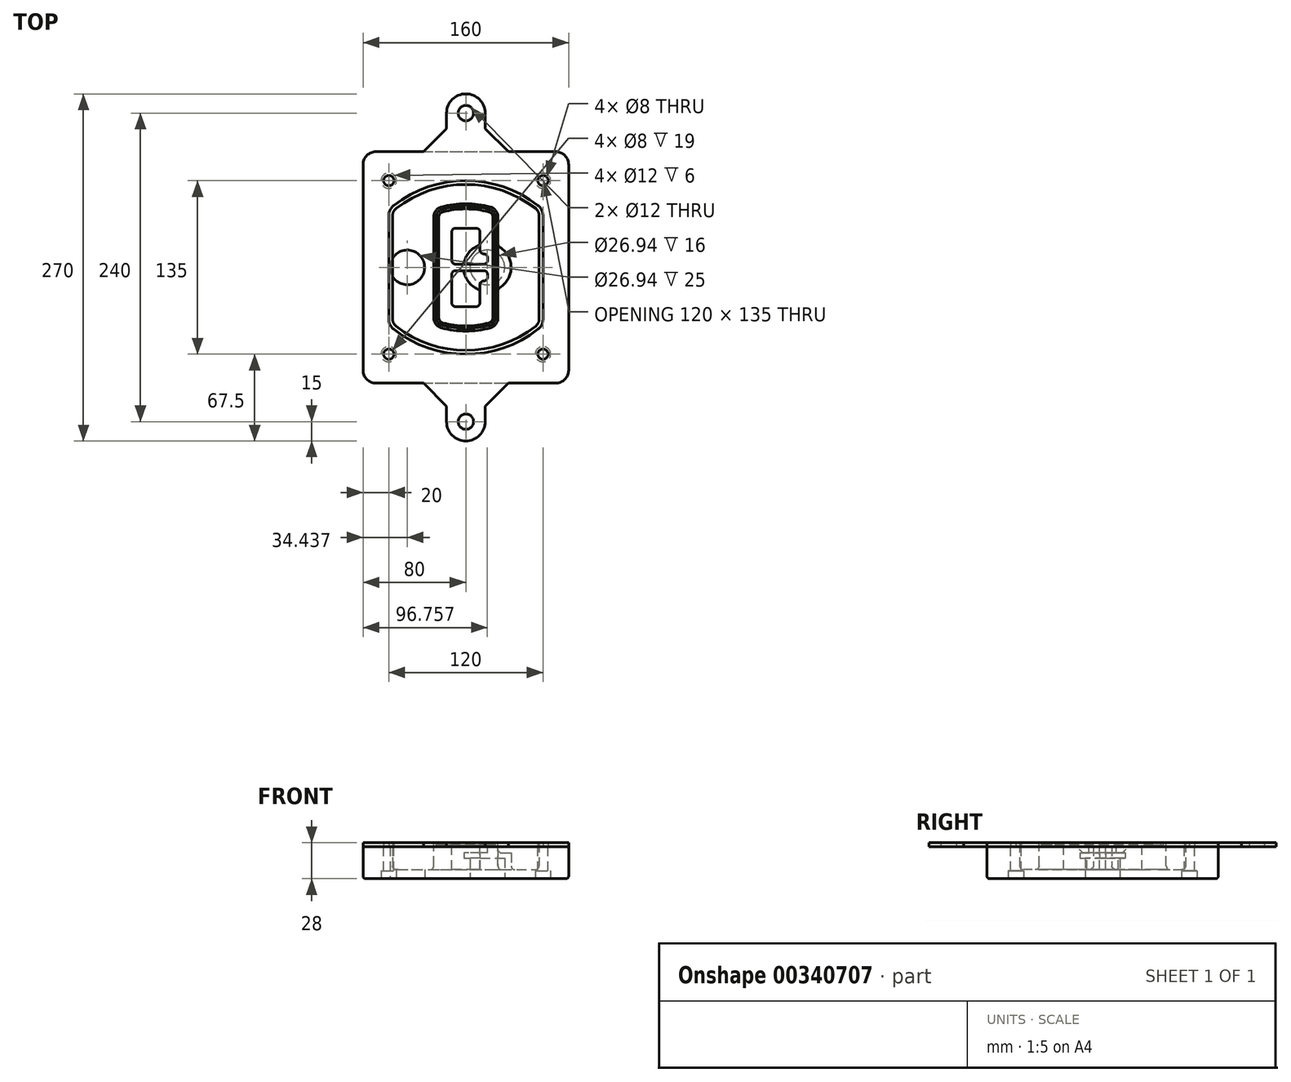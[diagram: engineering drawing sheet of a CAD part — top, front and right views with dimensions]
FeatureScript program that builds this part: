
annotation { "Feature Type Name" : "Feature", "Feature Type Description" : "" }
export const myFeature = defineFeature(function(context is Context, id is Id, definition is map)
    precondition{}
    {
        {
            var Q0;
            Q0=qCreatedBy(makeId("Top.planeOp"),FACE);
            var sketch = newSketch(context, id + "F0", { "sketchPlane" : qUnion([Q0])});
            skPoint(sketch, "E0.rect.middle", {"position": v(0, 0) * mm});
            skLineSegment(sketch, "E1.bottom", {"start": v(-70, -90) * mm, "end": v(70, -90) * mm});
            skLineSegment(sketch, "E1.top", {"start": v(-70, 90) * mm, "end": v(70, 90) * mm});
            skLineSegment(sketch, "E1.left", {"start": v(-80, -80) * mm, "end": v(-80, 80) * mm});
            skLineSegment(sketch, "E1.right", {"start": v(80, -80) * mm, "end": v(80, 80) * mm});
            skLineSegment(sketch, "E2", {"start": v(-80, 90) * mm, "end": v(80, -90) * mm, "construction": true});
            skLineSegment(sketch, "E3", {"start": v(80, 90) * mm, "end": v(-80, -90) * mm, "construction": true});
            skCircle(sketch, "E4", {"center": v(-60, 67.5) * mm, "radius": 4 * mm});
            skCircle(sketch, "E5", {"center": v(60, 67.5) * mm, "radius": 4 * mm});
            skCircle(sketch, "E6", {"center": v(60, -67.5) * mm, "radius": 4 * mm});
            skCircle(sketch, "E7", {"center": v(-60, -67.5) * mm, "radius": 4 * mm});
            skLineSegment(sketch, "E8", {"start": v(-60, 67.5) * mm, "end": v(60, 67.5) * mm, "construction": true});
            skLineSegment(sketch, "E9", {"start": v(60, 67.5) * mm, "end": v(60, -67.5) * mm, "construction": true});
            skLineSegment(sketch, "E10", {"start": v(60, -67.5) * mm, "end": v(-60, -67.5) * mm, "construction": true});
            skLineSegment(sketch, "E11", {"start": v(-60, -67.5) * mm, "end": v(-60, 67.5) * mm, "construction": true});
            skLineSegment(sketch, "E12", {"start": v(-60, 40.3) * mm, "end": v(-60, -40.3) * mm});
            skLineSegment(sketch, "E13", {"start": v(60, 40.3) * mm, "end": v(60, -40.3) * mm});
            skArc(sketch, "E14", {"start": v(56.15, 48.18) * mm, "mid": v(0, 67.5) * mm, "end": v(-56.15, 48.18) * mm});
            skArc(sketch, "E15", {"start": v(-56.15, -48.18) * mm, "mid": v(0, -67.5) * mm, "end": v(56.15, -48.18) * mm});
            skLineSegment(sketch, "E16", {"start": v(-60, 0) * mm, "end": v(60, 0) * mm, "construction": true});
            skPoint(sketch, "E17.visualSharp", {"position": v(-60, -45) * mm});
            skArc(sketch, "E17.filletArc", {"start": v(-60, -40.3) * mm, "mid": v(-58.99, -44.68) * mm, "end": v(-56.15, -48.18) * mm});
            skPoint(sketch, "E18.visualSharp", {"position": v(-60, 45) * mm});
            skArc(sketch, "E18.filletArc", {"start": v(-56.15, 48.18) * mm, "mid": v(-58.99, 44.68) * mm, "end": v(-60, 40.3) * mm});
            skPoint(sketch, "E19.visualSharp", {"position": v(60, 45) * mm});
            skArc(sketch, "E19.filletArc", {"start": v(60, 40.3) * mm, "mid": v(58.99, 44.68) * mm, "end": v(56.15, 48.18) * mm});
            skPoint(sketch, "E20.visualSharp", {"position": v(60, -45) * mm});
            skArc(sketch, "E20.filletArc", {"start": v(56.15, -48.18) * mm, "mid": v(58.99, -44.68) * mm, "end": v(60, -40.3) * mm});
            skPoint(sketch, "E21.visualSharp", {"position": v(-80, 90) * mm});
            skArc(sketch, "E21.filletArc", {"start": v(-70, 90) * mm, "mid": v(-77.07, 87.07) * mm, "end": v(-80, 80) * mm});
            skPoint(sketch, "E22.visualSharp", {"position": v(80, 90) * mm});
            skArc(sketch, "E22.filletArc", {"start": v(80, 80) * mm, "mid": v(77.07, 87.07) * mm, "end": v(70, 90) * mm});
            skPoint(sketch, "E23.visualSharp", {"position": v(80, -90) * mm});
            skArc(sketch, "E23.filletArc", {"start": v(70, -90) * mm, "mid": v(77.07, -87.07) * mm, "end": v(80, -80) * mm});
            skPoint(sketch, "E24.visualSharp", {"position": v(-80, -90) * mm});
            skArc(sketch, "E24.filletArc", {"start": v(-80, -80) * mm, "mid": v(-77.07, -87.07) * mm, "end": v(-70, -90) * mm});
            skArc(sketch, "E25.0", {"start": v(57, 40.3) * mm, "mid": v(56.3, 43.36) * mm, "end": v(54.3, 45.81) * mm});
            skLineSegment(sketch, "E25.1", {"start": v(57, 40.3) * mm, "end": v(57, -40.3) * mm});
            skArc(sketch, "E25.2", {"start": v(54.3, -45.81) * mm, "mid": v(56.3, -43.36) * mm, "end": v(57, -40.3) * mm});
            skArc(sketch, "E25.3", {"start": v(-54.3, -45.81) * mm, "mid": v(0, -64.5) * mm, "end": v(54.3, -45.81) * mm});
            skArc(sketch, "E25.4", {"start": v(-57, -40.3) * mm, "mid": v(-56.3, -43.36) * mm, "end": v(-54.3, -45.81) * mm});
            skArc(sketch, "E25.5", {"start": v(54.3, 45.81) * mm, "mid": v(0, 64.5) * mm, "end": v(-54.3, 45.81) * mm});
            skLineSegment(sketch, "E25.6", {"start": v(-57, 40.3) * mm, "end": v(-57, -40.3) * mm});
            skArc(sketch, "E25.7", {"start": v(-54.3, 45.81) * mm, "mid": v(-56.3, 43.36) * mm, "end": v(-57, 40.3) * mm});
            skArc(sketch, "E26.0", {"start": v(-58.62, 51.33) * mm, "mid": v(-62.58, 46.43) * mm, "end": v(-64, 40.3) * mm});
            skArc(sketch, "E26.1", {"start": v(58.62, 51.33) * mm, "mid": v(0, 71.5) * mm, "end": v(-58.62, 51.33) * mm});
            skArc(sketch, "E26.2", {"start": v(64, 40.3) * mm, "mid": v(62.58, 46.43) * mm, "end": v(58.62, 51.33) * mm});
            skLineSegment(sketch, "E26.3", {"start": v(64, 40.3) * mm, "end": v(64, -40.3) * mm});
            skArc(sketch, "E26.4", {"start": v(58.62, -51.33) * mm, "mid": v(62.58, -46.43) * mm, "end": v(64, -40.3) * mm});
            skLineSegment(sketch, "E26.5", {"start": v(-64, 40.3) * mm, "end": v(-64, -40.3) * mm});
            skArc(sketch, "E26.6", {"start": v(-58.62, -51.33) * mm, "mid": v(0, -71.5) * mm, "end": v(58.62, -51.33) * mm});
            skArc(sketch, "E26.7", {"start": v(-64, -40.3) * mm, "mid": v(-62.58, -46.43) * mm, "end": v(-58.62, -51.33) * mm});
            skSolve(sketch);
        }
        {
            var Q0;
            Q0=makeQuery(id+"F0.imprint","IMPRINT",FACE,{"disambiguationData":[TD([[makeQuery(id+"F0.imprint","IMPRINT",EDGE,{"derivedFrom":sQuery(id+"F0.wireOp",EDGE,"E1.bottom")}),1.0]])]});
            var Q1;
            Q1=makeQuery(id+"F0.imprint","IMPRINT",FACE,{"disambiguationData":[TD([[makeQuery(id+"F0.imprint","IMPRINT",EDGE,{"derivedFrom":sQuery(id+"F0.wireOp",EDGE,"E12")}),1.0]])]});
            var Q2;
            Q2=makeQuery(id+"F0.imprint","IMPRINT",FACE,{"disambiguationData":[TD([[makeQuery(id+"F0.imprint","IMPRINT",EDGE,{"derivedFrom":sQuery(id+"F0.wireOp",EDGE,"E25.0")}),1.0]])]});
            var Q3;
            Q3=makeQuery(id+"F0.imprint","IMPRINT",FACE,{"disambiguationData":[TD([[makeQuery(id+"F0.imprint","IMPRINT",EDGE,{"derivedFrom":sQuery(id+"F0.wireOp",EDGE,"E12")}),-1.0]])]});
            extrude(context, id + "F1", {"entities" : qUnion([Q0, Q1, Q2, Q3]), "oppositeDirection" : true, "depth" : 25 * mm});
        }
        {
            var Q0;
            Q0=makeQuery(id+"F0.imprint","IMPRINT",FACE,{"disambiguationData":[TD([[makeQuery(id+"F0.imprint","IMPRINT",EDGE,{"derivedFrom":sQuery(id+"F0.wireOp",EDGE,"E12")}),1.0]])]});
            extrude(context, id + "F2", {"entities" : qUnion([Q0]), "operationType" : NewBodyOperationType.ADD, "depth" : 3 * mm});
        }
        {
            var Q0;
            Q0=makeQuery(id+"F0.imprint","IMPRINT",FACE,{"disambiguationData":[TD([[makeQuery(id+"F0.imprint","IMPRINT",EDGE,{"derivedFrom":sQuery(id+"F0.wireOp",EDGE,"E25.0")}),1.0]])]});
            extrude(context, id + "F3", {"entities" : qUnion([Q0]), "operationType" : NewBodyOperationType.REMOVE, "oppositeDirection" : true, "depth" : 18 * mm});
        }
        {
            var Q0;
            Q0=makeQuery(id+"F2.opExtrude","CAP_FACE",FACE,{"disambiguationData":[OSD([sQuery(id+"F0.wireOp",EDGE,"E12"),sQuery(id+"F0.wireOp",EDGE,"E13"),sQuery(id+"F0.wireOp",EDGE,"E14"),sQuery(id+"F0.wireOp",EDGE,"E15"),sQuery(id+"F0.wireOp",EDGE,"E17.filletArc"),sQuery(id+"F0.wireOp",EDGE,"E18.filletArc"),sQuery(id+"F0.wireOp",EDGE,"E19.filletArc"),sQuery(id+"F0.wireOp",EDGE,"E20.filletArc"),sQuery(id+"F0.wireOp",EDGE,"E25.0"),sQuery(id+"F0.wireOp",EDGE,"E25.1"),sQuery(id+"F0.wireOp",EDGE,"E25.2"),sQuery(id+"F0.wireOp",EDGE,"E25.3"),sQuery(id+"F0.wireOp",EDGE,"E25.4"),sQuery(id+"F0.wireOp",EDGE,"E25.5"),sQuery(id+"F0.wireOp",EDGE,"E25.6"),sQuery(id+"F0.wireOp",EDGE,"E25.7")])],"isStart":false});
            var sketch = newSketch(context, id + "F4", { "sketchPlane" : qUnion([Q0])});
            skArc(sketch, "E27.0", {"start": v(-19.08, -46.97) * mm, "mid": v(0, -49.5) * mm, "end": v(19.08, -46.97) * mm});
            skArc(sketch, "E28.0", {"start": v(19.08, 46.97) * mm, "mid": v(0, 49.5) * mm, "end": v(-19.08, 46.97) * mm});
            skLineSegment(sketch, "E29", {"start": v(-25, 39.25) * mm, "end": v(-25, -39.25) * mm});
            skLineSegment(sketch, "E30", {"start": v(25, 39.25) * mm, "end": v(25, -39.25) * mm});
            skLineSegment(sketch, "E31", {"start": v(-25, 45.1) * mm, "end": v(25, 45.1) * mm, "construction": true});
            skLineSegment(sketch, "E32", {"start": v(-25, -45.1) * mm, "end": v(25, -45.1) * mm, "construction": true});
            skPoint(sketch, "E33.visualSharp", {"position": v(-25, 45.1) * mm});
            skArc(sketch, "E33.filletArc", {"start": v(-19.08, 46.97) * mm, "mid": v(-23.35, 44.11) * mm, "end": v(-25, 39.25) * mm});
            skPoint(sketch, "E34.visualSharp", {"position": v(25, 45.1) * mm});
            skArc(sketch, "E34.filletArc", {"start": v(25, 39.25) * mm, "mid": v(23.35, 44.11) * mm, "end": v(19.08, 46.97) * mm});
            skPoint(sketch, "E35.visualSharp", {"position": v(25, -45.1) * mm});
            skArc(sketch, "E35.filletArc", {"start": v(19.08, -46.97) * mm, "mid": v(23.35, -44.11) * mm, "end": v(25, -39.25) * mm});
            skPoint(sketch, "E36.visualSharp", {"position": v(-25, -45.1) * mm});
            skArc(sketch, "E36.filletArc", {"start": v(-25, -39.25) * mm, "mid": v(-23.35, -44.11) * mm, "end": v(-19.08, -46.97) * mm});
            skArc(sketch, "E37.0", {"start": v(54.3, 45.81) * mm, "mid": v(0, 64.5) * mm, "end": v(-54.3, 45.81) * mm});
            skArc(sketch, "E37.1", {"start": v(-54.3, 45.81) * mm, "mid": v(-56.3, 43.36) * mm, "end": v(-57, 40.3) * mm});
            skLineSegment(sketch, "E37.2", {"start": v(-57, 40.3) * mm, "end": v(-57, -40.3) * mm});
            skArc(sketch, "E37.3", {"start": v(-57, -40.3) * mm, "mid": v(-56.3, -43.36) * mm, "end": v(-54.3, -45.81) * mm});
            skArc(sketch, "E37.4", {"start": v(-54.3, -45.81) * mm, "mid": v(0, -64.5) * mm, "end": v(54.3, -45.81) * mm});
            skArc(sketch, "E37.5", {"start": v(54.3, -45.81) * mm, "mid": v(56.3, -43.36) * mm, "end": v(57, -40.3) * mm});
            skLineSegment(sketch, "E37.6", {"start": v(57, 40.3) * mm, "end": v(57, -40.3) * mm});
            skArc(sketch, "E37.7", {"start": v(57, 40.3) * mm, "mid": v(56.3, 43.36) * mm, "end": v(54.3, 45.81) * mm});
            skLineSegment(sketch, "E38.0", {"start": v(23, 39.25) * mm, "end": v(23, -39.25) * mm});
            skArc(sketch, "E38.1", {"start": v(18.56, -45.04) * mm, "mid": v(21.76, -42.9) * mm, "end": v(23, -39.25) * mm});
            skArc(sketch, "E38.2", {"start": v(-18.56, -45.04) * mm, "mid": v(0, -47.5) * mm, "end": v(18.56, -45.04) * mm});
            skArc(sketch, "E38.3", {"start": v(-23, -39.25) * mm, "mid": v(-21.76, -42.9) * mm, "end": v(-18.56, -45.04) * mm});
            skLineSegment(sketch, "E38.4", {"start": v(-23, 39.25) * mm, "end": v(-23, -39.25) * mm});
            skArc(sketch, "E38.5", {"start": v(23, 39.25) * mm, "mid": v(21.76, 42.9) * mm, "end": v(18.56, 45.04) * mm});
            skArc(sketch, "E38.6", {"start": v(-18.56, 45.04) * mm, "mid": v(-21.76, 42.9) * mm, "end": v(-23, 39.25) * mm});
            skArc(sketch, "E38.7", {"start": v(18.56, 45.04) * mm, "mid": v(0, 47.5) * mm, "end": v(-18.56, 45.04) * mm});
            skArc(sketch, "E39.0", {"start": v(21, 39.25) * mm, "mid": v(20.18, 41.68) * mm, "end": v(18.04, 43.1) * mm});
            skLineSegment(sketch, "E39.1", {"start": v(21, 39.25) * mm, "end": v(21, -39.25) * mm});
            skArc(sketch, "E39.2", {"start": v(18.04, -43.1) * mm, "mid": v(20.18, -41.68) * mm, "end": v(21, -39.25) * mm});
            skArc(sketch, "E39.3", {"start": v(-18.04, -43.1) * mm, "mid": v(0, -45.5) * mm, "end": v(18.04, -43.1) * mm});
            skArc(sketch, "E39.4", {"start": v(-21, -39.25) * mm, "mid": v(-20.18, -41.68) * mm, "end": v(-18.04, -43.1) * mm});
            skArc(sketch, "E39.5", {"start": v(18.04, 43.1) * mm, "mid": v(0, 45.5) * mm, "end": v(-18.04, 43.1) * mm});
            skLineSegment(sketch, "E39.6", {"start": v(-21, 39.25) * mm, "end": v(-21, -39.25) * mm});
            skArc(sketch, "E39.7", {"start": v(-18.04, 43.1) * mm, "mid": v(-20.18, 41.68) * mm, "end": v(-21, 39.25) * mm});
            skLineSegment(sketch, "E40", {"start": v(-25, 0) * mm, "end": v(25, 0) * mm, "construction": true});
            skLineSegment(sketch, "E41", {"start": v(-11, 5.5) * mm, "end": v(-11, 27.5) * mm});
            skLineSegment(sketch, "E42", {"start": v(-8, 30.5) * mm, "end": v(8, 30.5) * mm});
            skLineSegment(sketch, "E43", {"start": v(11, 27.5) * mm, "end": v(11, 13.5) * mm});
            skLineSegment(sketch, "E44", {"start": v(14, 10.5) * mm, "end": v(14, 10.5) * mm});
            skLineSegment(sketch, "E45", {"start": v(17, 7.5) * mm, "end": v(17, 5.5) * mm});
            skLineSegment(sketch, "E46", {"start": v(14, 2.5) * mm, "end": v(-8, 2.5) * mm});
            skPoint(sketch, "E47.visualSharp", {"position": v(-11, 30.5) * mm});
            skArc(sketch, "E47.filletArc", {"start": v(-8, 30.5) * mm, "mid": v(-10.12, 29.62) * mm, "end": v(-11, 27.5) * mm});
            skPoint(sketch, "E48.visualSharp", {"position": v(11, 30.5) * mm});
            skArc(sketch, "E48.filletArc", {"start": v(11, 27.5) * mm, "mid": v(10.12, 29.62) * mm, "end": v(8, 30.5) * mm});
            skPoint(sketch, "E49.visualSharp", {"position": v(11, 10.5) * mm});
            skArc(sketch, "E49.filletArc", {"start": v(11, 13.5) * mm, "mid": v(11.88, 11.38) * mm, "end": v(14, 10.5) * mm});
            skPoint(sketch, "E50.visualSharp", {"position": v(17, 10.5) * mm});
            skArc(sketch, "E50.filletArc", {"start": v(17, 7.5) * mm, "mid": v(16.12, 9.62) * mm, "end": v(14, 10.5) * mm});
            skPoint(sketch, "E51.visualSharp", {"position": v(17, 2.5) * mm});
            skArc(sketch, "E51.filletArc", {"start": v(14, 2.5) * mm, "mid": v(16.12, 3.38) * mm, "end": v(17, 5.5) * mm});
            skPoint(sketch, "E52.visualSharp", {"position": v(-11, 2.5) * mm});
            skArc(sketch, "E52.filletArc", {"start": v(-11, 5.5) * mm, "mid": v(-10.12, 3.38) * mm, "end": v(-8, 2.5) * mm});
            skLineSegment(sketch, "E53.0.MirrorCS", {"start": v(14, -2.5) * mm, "end": v(-8, -2.5) * mm});
            skArc(sketch, "E54.0.MirrorCS", {"start": v(-11, -5.5) * mm, "mid": v(-10.12, -3.38) * mm, "end": v(-8, -2.5) * mm});
            skLineSegment(sketch, "E55.0.MirrorCS", {"start": v(-11, -5.5) * mm, "end": v(-11, -27.5) * mm});
            skArc(sketch, "E56.0.MirrorCS", {"start": v(-8, -30.5) * mm, "mid": v(-10.12, -29.62) * mm, "end": v(-11, -27.5) * mm});
            skLineSegment(sketch, "E57.0.MirrorCS", {"start": v(-8, -30.5) * mm, "end": v(8, -30.5) * mm});
            skArc(sketch, "E58.0.MirrorCS", {"start": v(11, -27.5) * mm, "mid": v(10.12, -29.62) * mm, "end": v(8, -30.5) * mm});
            skLineSegment(sketch, "E59.0.MirrorCS", {"start": v(11, -27.5) * mm, "end": v(11, -13.5) * mm});
            skArc(sketch, "E60.0.MirrorCS", {"start": v(11, -13.5) * mm, "mid": v(11.88, -11.38) * mm, "end": v(14, -10.5) * mm});
            skArc(sketch, "E61.0.MirrorCS", {"start": v(17, -7.5) * mm, "mid": v(16.12, -9.62) * mm, "end": v(14, -10.5) * mm});
            skLineSegment(sketch, "E62.0.MirrorCS", {"start": v(17, -7.5) * mm, "end": v(17, -5.5) * mm});
            skArc(sketch, "E63.0.MirrorCS", {"start": v(14, -2.5) * mm, "mid": v(16.12, -3.38) * mm, "end": v(17, -5.5) * mm});
            skSolve(sketch);
        }
        {
            var Q0;
            Q0=makeQuery(id+"F4.imprint","IMPRINT",FACE,{"disambiguationData":[TD([[makeQuery(id+"F4.imprint","IMPRINT",EDGE,{"derivedFrom":sQuery(id+"F4.wireOp",EDGE,"E27.0")}),1.0]])]});
            var Q1;
            Q1=makeQuery(id+"F4.imprint","IMPRINT",FACE,{"disambiguationData":[TD([[makeQuery(id+"F4.imprint","IMPRINT",EDGE,{"derivedFrom":sQuery(id+"F4.wireOp",EDGE,"E38.0")}),-1.0]])]});
            var Q2;
            Q2=makeQuery(id+"F4.imprint","IMPRINT",FACE,{"disambiguationData":[TD([[makeQuery(id+"F4.imprint","IMPRINT",EDGE,{"derivedFrom":sQuery(id+"F4.wireOp",EDGE,"E39.0")}),1.0]])]});
            extrude(context, id + "F5", {"entities" : qUnion([Q0, Q1, Q2]), "operationType" : NewBodyOperationType.ADD, "endBound" : BoundingType.UP_TO_NEXT, "oppositeDirection" : true, "depth" : 25 * mm});
        }
        {
            var Q0;
            Q0=makeQuery(id+"F4.imprint","IMPRINT",FACE,{"disambiguationData":[TD([[makeQuery(id+"F4.imprint","IMPRINT",EDGE,{"derivedFrom":sQuery(id+"F4.wireOp",EDGE,"E38.0")}),-1.0]])]});
            extrude(context, id + "F6", {"entities" : qUnion([Q0]), "operationType" : NewBodyOperationType.REMOVE, "oppositeDirection" : true, "depth" : 2 * mm});
        }
        {
            var Q0;
            Q0=makeQuery(id+"F1.opExtrude","CAP_FACE",FACE,{"disambiguationData":[OSD([sQuery(id+"F0.wireOp",EDGE,"E1.bottom"),sQuery(id+"F0.wireOp",EDGE,"E1.top"),sQuery(id+"F0.wireOp",EDGE,"E1.left"),sQuery(id+"F0.wireOp",EDGE,"E1.right"),sQuery(id+"F0.wireOp",EDGE,"E4"),sQuery(id+"F0.wireOp",EDGE,"E5"),sQuery(id+"F0.wireOp",EDGE,"E6"),sQuery(id+"F0.wireOp",EDGE,"E7"),sQuery(id+"F0.wireOp",EDGE,"E21.filletArc"),sQuery(id+"F0.wireOp",EDGE,"E22.filletArc"),sQuery(id+"F0.wireOp",EDGE,"E23.filletArc"),sQuery(id+"F0.wireOp",EDGE,"E24.filletArc")])],"isStart":false});
            var sketch = newSketch(context, id + "F7", { "sketchPlane" : qUnion([Q0])});
            skCircle(sketch, "E64", {"center": v(16.76, 0) * mm, "radius": 13.47 * mm});
            skCircle(sketch, "E65", {"center": v(-45.56, 0) * mm, "radius": 13.47 * mm});
            skLineSegment(sketch, "E66", {"start": v(80, 0) * mm, "end": v(-80, 0) * mm});
            skCircle(sketch, "E67", {"center": v(16.76, 0) * mm, "radius": 18.47 * mm});
            skCircle(sketch, "E68", {"center": v(60, -67.5) * mm, "radius": 6 * mm});
            skCircle(sketch, "E69", {"center": v(-60, -67.5) * mm, "radius": 6 * mm});
            skCircle(sketch, "E70", {"center": v(-60, 67.5) * mm, "radius": 6 * mm});
            skCircle(sketch, "E71", {"center": v(60, 67.5) * mm, "radius": 6 * mm});
            skSolve(sketch);
        }
        {
            var Q0;
            {var subQ1=sQuery(id+"F7.wireOp",EDGE,"E66");var subQ4=sQuery(id+"F7.wireOp",EDGE,"E64");var subQ6=makeQuery(id+"F7.imprint","INTERSECT",VERTEX,{"disambiguationData":[OD(0.0)],"derivedFrom":[subQ4,subQ1]});Q0=makeQuery(id+"F7.imprint","IMPRINT",FACE,{"disambiguationData":[TD([[makeQuery(id+"F7.imprint","IMPRINT",EDGE,{"disambiguationData":[TD([[subQ6,-1.0]])],"derivedFrom":subQ4}),-1.0]])]});}
            var Q1;
            {var subQ0=sQuery(id+"F7.wireOp",EDGE,"E66");var subQ1=sQuery(id+"F7.wireOp",EDGE,"E64");var subQ3=makeQuery(id+"F7.imprint","INTERSECT",VERTEX,{"disambiguationData":[OD(0.0)],"derivedFrom":[subQ1,subQ0]});Q1=makeQuery(id+"F7.imprint","IMPRINT",FACE,{"disambiguationData":[TD([[makeQuery(id+"F7.imprint","IMPRINT",EDGE,{"disambiguationData":[TD([[subQ3,-1.0]])],"derivedFrom":subQ1}),1.0]])]});}
            var Q2;
            {var subQ0=sQuery(id+"F7.wireOp",EDGE,"E66");var subQ1=sQuery(id+"F7.wireOp",EDGE,"E64");var subQ3=makeQuery(id+"F7.imprint","INTERSECT",VERTEX,{"disambiguationData":[OD(0.0)],"derivedFrom":[subQ1,subQ0]});Q2=makeQuery(id+"F7.imprint","IMPRINT",FACE,{"disambiguationData":[TD([[makeQuery(id+"F7.imprint","IMPRINT",EDGE,{"disambiguationData":[TD([[subQ3,1.0]])],"derivedFrom":subQ1}),1.0]])]});}
            var Q3;
            {var subQ1=sQuery(id+"F7.wireOp",EDGE,"E66");var subQ4=sQuery(id+"F7.wireOp",EDGE,"E64");var subQ6=makeQuery(id+"F7.imprint","INTERSECT",VERTEX,{"disambiguationData":[OD(0.0)],"derivedFrom":[subQ4,subQ1]});Q3=makeQuery(id+"F7.imprint","IMPRINT",FACE,{"disambiguationData":[TD([[makeQuery(id+"F7.imprint","IMPRINT",EDGE,{"disambiguationData":[TD([[subQ6,1.0]])],"derivedFrom":subQ4}),-1.0]])]});}
            extrude(context, id + "F8", {"entities" : qUnion([Q0, Q1, Q2, Q3]), "operationType" : NewBodyOperationType.ADD, "oppositeDirection" : true, "depth" : 20 * mm});
        }
        {
            var Q0;
            {var subQ0=sQuery(id+"F7.wireOp",EDGE,"E66");var subQ1=sQuery(id+"F7.wireOp",EDGE,"E64");var subQ3=makeQuery(id+"F7.imprint","INTERSECT",VERTEX,{"disambiguationData":[OD(0.0)],"derivedFrom":[subQ1,subQ0]});Q0=makeQuery(id+"F7.imprint","IMPRINT",FACE,{"disambiguationData":[TD([[makeQuery(id+"F7.imprint","IMPRINT",EDGE,{"disambiguationData":[TD([[subQ3,-1.0]])],"derivedFrom":subQ1}),1.0]])]});}
            var Q1;
            {var subQ0=sQuery(id+"F7.wireOp",EDGE,"E66");var subQ1=sQuery(id+"F7.wireOp",EDGE,"E64");var subQ3=makeQuery(id+"F7.imprint","INTERSECT",VERTEX,{"disambiguationData":[OD(0.0)],"derivedFrom":[subQ1,subQ0]});Q1=makeQuery(id+"F7.imprint","IMPRINT",FACE,{"disambiguationData":[TD([[makeQuery(id+"F7.imprint","IMPRINT",EDGE,{"disambiguationData":[TD([[subQ3,1.0]])],"derivedFrom":subQ1}),1.0]])]});}
            extrude(context, id + "F9", {"entities" : qUnion([Q0, Q1]), "operationType" : NewBodyOperationType.REMOVE, "oppositeDirection" : true, "depth" : 16 * mm});
        }
        {
            var Q0;
            {var subQ0=sQuery(id+"F7.wireOp",EDGE,"E66");var subQ1=sQuery(id+"F7.wireOp",EDGE,"E65");var subQ3=makeQuery(id+"F7.imprint","INTERSECT",VERTEX,{"disambiguationData":[OD(0.0)],"derivedFrom":[subQ1,subQ0]});Q0=makeQuery(id+"F7.imprint","IMPRINT",FACE,{"disambiguationData":[TD([[makeQuery(id+"F7.imprint","IMPRINT",EDGE,{"disambiguationData":[TD([[subQ3,-1.0]])],"derivedFrom":subQ1}),1.0]])]});}
            var Q1;
            {var subQ0=sQuery(id+"F7.wireOp",EDGE,"E66");var subQ1=sQuery(id+"F7.wireOp",EDGE,"E65");var subQ3=makeQuery(id+"F7.imprint","INTERSECT",VERTEX,{"disambiguationData":[OD(0.0)],"derivedFrom":[subQ1,subQ0]});Q1=makeQuery(id+"F7.imprint","IMPRINT",FACE,{"disambiguationData":[TD([[makeQuery(id+"F7.imprint","IMPRINT",EDGE,{"disambiguationData":[TD([[subQ3,1.0]])],"derivedFrom":subQ1}),1.0]])]});}
            extrude(context, id + "F10", {"entities" : qUnion([Q0, Q1]), "operationType" : NewBodyOperationType.REMOVE, "oppositeDirection" : true, "depth" : 25 * mm});
        }
        {
            var Q0;
            Q0=makeQuery(id+"F7.imprint","IMPRINT",FACE,{"disambiguationData":[TD([[makeQuery(id+"F7.imprint","IMPRINT",EDGE,{"derivedFrom":sQuery(id+"F7.wireOp",EDGE,"E68")}),1.0]])]});
            var Q1;
            Q1=makeQuery(id+"F7.imprint","IMPRINT",FACE,{"disambiguationData":[TD([[makeQuery(id+"F7.imprint","IMPRINT",EDGE,{"derivedFrom":makeQuery(id+"F1.opExtrude","CAP_EDGE",EDGE,{"disambiguationData":[OSD([sQuery(id+"F0.wireOp",EDGE,"E5")])],"isStart":false})}),-1.0]])]});
            var Q2;
            Q2=makeQuery(id+"F7.imprint","IMPRINT",FACE,{"disambiguationData":[TD([[makeQuery(id+"F7.imprint","IMPRINT",EDGE,{"derivedFrom":sQuery(id+"F7.wireOp",EDGE,"E69")}),1.0]])]});
            var Q3;
            Q3=makeQuery(id+"F7.imprint","IMPRINT",FACE,{"disambiguationData":[TD([[makeQuery(id+"F7.imprint","IMPRINT",EDGE,{"derivedFrom":makeQuery(id+"F1.opExtrude","CAP_EDGE",EDGE,{"disambiguationData":[OSD([sQuery(id+"F0.wireOp",EDGE,"E4")])],"isStart":false})}),-1.0]])]});
            var Q4;
            Q4=makeQuery(id+"F7.imprint","IMPRINT",FACE,{"disambiguationData":[TD([[makeQuery(id+"F7.imprint","IMPRINT",EDGE,{"derivedFrom":sQuery(id+"F7.wireOp",EDGE,"E70")}),1.0]])]});
            var Q5;
            Q5=makeQuery(id+"F7.imprint","IMPRINT",FACE,{"disambiguationData":[TD([[makeQuery(id+"F7.imprint","IMPRINT",EDGE,{"derivedFrom":makeQuery(id+"F1.opExtrude","CAP_EDGE",EDGE,{"disambiguationData":[OSD([sQuery(id+"F0.wireOp",EDGE,"E7")])],"isStart":false})}),-1.0]])]});
            var Q6;
            Q6=makeQuery(id+"F7.imprint","IMPRINT",FACE,{"disambiguationData":[TD([[makeQuery(id+"F7.imprint","IMPRINT",EDGE,{"derivedFrom":sQuery(id+"F7.wireOp",EDGE,"E71")}),1.0]])]});
            var Q7;
            Q7=makeQuery(id+"F7.imprint","IMPRINT",FACE,{"disambiguationData":[TD([[makeQuery(id+"F7.imprint","IMPRINT",EDGE,{"derivedFrom":makeQuery(id+"F1.opExtrude","CAP_EDGE",EDGE,{"disambiguationData":[OSD([sQuery(id+"F0.wireOp",EDGE,"E6")])],"isStart":false})}),-1.0]])]});
            extrude(context, id + "F11", {"entities" : qUnion([Q0, Q1, Q2, Q3, Q4, Q5, Q6, Q7]), "operationType" : NewBodyOperationType.REMOVE, "oppositeDirection" : true, "depth" : 6 * mm});
        }
        {
            var Q0;
            Q0=makeQuery(id+"F9.boolean.opBoolean","COPY",FACE,{"derivedFrom":makeQuery(id+"F9.opExtrude","CAP_FACE",FACE,{"disambiguationData":[OSD([sQuery(id+"F7.wireOp",EDGE,"E64")])],"isStart":false})});
            var sketch = newSketch(context, id + "F12", { "sketchPlane" : qUnion([Q0])});
            skArc(sketch, "E72.0", {"start": v(11, 17.55) * mm, "mid": v(2.57, 11.82) * mm, "end": v(-1.54, 2.5) * mm});
            skArc(sketch, "E72.1", {"start": v(-1.54, -2.5) * mm, "mid": v(2.57, -11.82) * mm, "end": v(11, -17.55) * mm});
            skLineSegment(sketch, "E73", {"start": v(-1.54, -2.5) * mm, "end": v(14, -2.5) * mm});
            skLineSegment(sketch, "E74.0", {"start": v(14, 2.5) * mm, "end": v(-1.54, 2.5) * mm});
            skArc(sketch, "E74.1", {"start": v(14, 2.5) * mm, "mid": v(16.12, 3.38) * mm, "end": v(17, 5.5) * mm});
            skLineSegment(sketch, "E74.2", {"start": v(17, 7.5) * mm, "end": v(17, 5.5) * mm});
            skArc(sketch, "E74.3", {"start": v(17, 7.5) * mm, "mid": v(16.12, 9.62) * mm, "end": v(14, 10.5) * mm});
            skArc(sketch, "E74.4", {"start": v(11, 13.5) * mm, "mid": v(11.88, 11.38) * mm, "end": v(14, 10.5) * mm});
            skLineSegment(sketch, "E74.5", {"start": v(11, 17.55) * mm, "end": v(11, 13.5) * mm});
            skLineSegment(sketch, "E74.7", {"start": v(14, -2.5) * mm, "end": v(-1.54, -2.5) * mm});
            skArc(sketch, "E74.8", {"start": v(14, -2.5) * mm, "mid": v(16.12, -3.38) * mm, "end": v(17, -5.5) * mm});
            skLineSegment(sketch, "E74.9", {"start": v(17, -7.5) * mm, "end": v(17, -5.5) * mm});
            skArc(sketch, "E74.10", {"start": v(17, -7.5) * mm, "mid": v(16.12, -9.62) * mm, "end": v(14, -10.5) * mm});
            skArc(sketch, "E74.11", {"start": v(11, -13.5) * mm, "mid": v(11.88, -11.38) * mm, "end": v(14, -10.5) * mm});
            skLineSegment(sketch, "E74.12", {"start": v(11, -17.55) * mm, "end": v(11, -13.5) * mm});
            skPoint(sketch, "E75.orphan", {"position": v(11, -27.5) * mm});
            skPoint(sketch, "E76.orphan", {"position": v(-8, -2.5) * mm});
            skPoint(sketch, "E77.orphan", {"position": v(-8, 2.5) * mm});
            skPoint(sketch, "E78.orphan", {"position": v(11, 27.5) * mm});
            skSolve(sketch);
        }
        {
            var Q0;
            {var subQ7=sQuery(id+"F12.wireOp",EDGE,"E72.0");var subQ14=sQuery(id+"F12.wireOp",EDGE,"E72.1");var subQ16=sQuery(id+"F12.wireOp",EDGE,"E74.1");var subQ18=sQuery(id+"F12.wireOp",EDGE,"E74.8");Q0=qUnion([makeQuery(id+"F12.imprint","IMPRINT",FACE,{"disambiguationData":[TD([[makeQuery(id+"F12.imprint","IMPRINT",EDGE,{"derivedFrom":subQ7}),1.0]])]}),makeQuery(id+"F12.imprint","IMPRINT",FACE,{"disambiguationData":[TD([[makeQuery(id+"F12.imprint","IMPRINT",EDGE,{"derivedFrom":subQ14}),1.0]])]}),makeQuery(id+"F12.imprint","IMPRINT",FACE,{"disambiguationData":[TD([[makeQuery(id+"F12.imprint","IMPRINT",EDGE,{"derivedFrom":subQ16}),1.0]])]}),makeQuery(id+"F12.imprint","IMPRINT",FACE,{"disambiguationData":[TD([[makeQuery(id+"F12.imprint","IMPRINT",EDGE,{"derivedFrom":subQ18}),-1.0]])]})]);}
            var Q1;
            Q1=makeQuery(id+"F5.boolean.opBoolean","SPLIT",FACE,{"disambiguationData":[TD([makeQuery(id+"F5.opExtrude","SWEPT_FACE",FACE,{"disambiguationData":[OSD([sQuery(id+"F4.wireOp",EDGE,"E41")])]})])],"derivedFrom":makeQuery(id+"F3.boolean.opBoolean","COPY",FACE,{"derivedFrom":makeQuery(id+"F3.opExtrude","CAP_FACE",FACE,{"disambiguationData":[OSD([sQuery(id+"F0.wireOp",EDGE,"E25.0"),sQuery(id+"F0.wireOp",EDGE,"E25.1"),sQuery(id+"F0.wireOp",EDGE,"E25.2"),sQuery(id+"F0.wireOp",EDGE,"E25.3"),sQuery(id+"F0.wireOp",EDGE,"E25.4"),sQuery(id+"F0.wireOp",EDGE,"E25.5"),sQuery(id+"F0.wireOp",EDGE,"E25.6"),sQuery(id+"F0.wireOp",EDGE,"E25.7")])],"isStart":false})})});
            extrude(context, id + "F13", {"entities" : qUnion([Q0]), "operationType" : NewBodyOperationType.REMOVE, "endBound" : BoundingType.UP_TO_SURFACE, "endBoundEntityFace" : qUnion([Q1]), "depth" : 25 * mm});
        }
        {
            var Q0;
            Q0=makeQuery(id+"F3.boolean.opBoolean","COPY",EDGE,{"derivedFrom":makeQuery(id+"F3.opExtrude","CAP_EDGE",EDGE,{"disambiguationData":[OSD([sQuery(id+"F0.wireOp",EDGE,"E25.6")])],"isStart":false})});
            var Q1;
            Q1=makeQuery(id+"F8.boolean.opBoolean","INTERSECT",EDGE,{"derivedFrom":[makeQuery(id+"F5.opExtrude","SWEPT_FACE",FACE,{"disambiguationData":[OSD([sQuery(id+"F4.wireOp",EDGE,"E30")])]}),makeQuery(id+"F8.opExtrude","CAP_FACE",FACE,{"disambiguationData":[OSD([sQuery(id+"F7.wireOp",EDGE,"E67")])],"isStart":false})]});
            var Q2;
            Q2=makeQuery(id+"F8.boolean.opBoolean","INTERSECT",EDGE,{"disambiguationData":[OD(1.0)],"derivedFrom":[makeQuery(id+"F5.opExtrude","SWEPT_FACE",FACE,{"disambiguationData":[OSD([sQuery(id+"F4.wireOp",EDGE,"E30")])]}),makeQuery(id+"F8.opExtrude","SWEPT_FACE",FACE,{"disambiguationData":[OSD([sQuery(id+"F7.wireOp",EDGE,"E67")])]})]});
            var Q3;
            {var subQ0=sQuery(id+"F4.wireOp",EDGE,"E30");Q3=makeQuery(id+"F8.boolean.opBoolean","SPLIT",EDGE,{"disambiguationData":[TD([makeQuery(id+"F5.opExtrude","SWEPT_FACE",FACE,{"disambiguationData":[OSD([sQuery(id+"F4.wireOp",EDGE,"E35.filletArc")])]})])],"derivedFrom":makeQuery(id+"F5.opExtrude","CAP_EDGE",EDGE,{"disambiguationData":[OSD([subQ0])],"isStart":false})});}
            var Q4;
            {var subQ0=sQuery(id+"F0.wireOp",EDGE,"E25.7");var subQ1=sQuery(id+"F0.wireOp",EDGE,"E25.1");var subQ2=sQuery(id+"F0.wireOp",EDGE,"E25.6");var subQ3=sQuery(id+"F0.wireOp",EDGE,"E25.5");var subQ4=sQuery(id+"F0.wireOp",EDGE,"E25.4");var subQ5=sQuery(id+"F0.wireOp",EDGE,"E25.0");var subQ6=sQuery(id+"F0.wireOp",EDGE,"E25.2");var subQ7=sQuery(id+"F0.wireOp",EDGE,"E25.3");Q4=makeQuery(id+"F8.boolean.opBoolean","INTERSECT",EDGE,{"derivedFrom":[makeQuery(id+"F5.boolean.opBoolean","SPLIT",FACE,{"disambiguationData":[TD([makeQuery(id+"F2.opExtrude","SWEPT_FACE",FACE,{"disambiguationData":[OSD([subQ5])]})])],"derivedFrom":makeQuery(id+"F3.boolean.opBoolean","COPY",FACE,{"derivedFrom":makeQuery(id+"F3.opExtrude","CAP_FACE",FACE,{"disambiguationData":[OSD([subQ5,subQ1,subQ6,subQ7,subQ4,subQ3,subQ2,subQ0])],"isStart":false})})}),makeQuery(id+"F8.opExtrude","SWEPT_FACE",FACE,{"disambiguationData":[OSD([sQuery(id+"F7.wireOp",EDGE,"E67")])]})]});}
            var Q5;
            Q5=makeQuery(id+"F8.boolean.opBoolean","INTERSECT",EDGE,{"disambiguationData":[OD(0.0)],"derivedFrom":[makeQuery(id+"F5.opExtrude","SWEPT_FACE",FACE,{"disambiguationData":[OSD([sQuery(id+"F4.wireOp",EDGE,"E30")])]}),makeQuery(id+"F8.opExtrude","SWEPT_FACE",FACE,{"disambiguationData":[OSD([sQuery(id+"F7.wireOp",EDGE,"E67")])]})]});
            fillet(context, id + "F14", {"entities" : qUnion([Q0, Q1, Q2, Q3, Q4, Q5]), "radius" : 3 * mm, "tangentPropagation" : true, "allowEdgeOverflow" : false});
        }
        {
            var Q0;
            Q0=makeQuery(id+"F1.opExtrude","CAP_EDGE",EDGE,{"disambiguationData":[OSD([sQuery(id+"F0.wireOp",EDGE,"E1.bottom")])],"isStart":false});
            fillet(context, id + "F15", {"entities" : qUnion([Q0]), "radius" : 2 * mm, "tangentPropagation" : true, "allowEdgeOverflow" : false});
        }
        {
            var Q0;
            {var subQ0=sQuery(id+"F0.wireOp",EDGE,"E21.filletArc");var subQ1=sQuery(id+"F0.wireOp",EDGE,"E7");var subQ2=sQuery(id+"F0.wireOp",EDGE,"E6");var subQ3=sQuery(id+"F0.wireOp",EDGE,"E5");var subQ4=sQuery(id+"F0.wireOp",EDGE,"E4");var subQ5=sQuery(id+"F0.wireOp",EDGE,"E22.filletArc");var subQ6=sQuery(id+"F0.wireOp",EDGE,"E1.bottom");var subQ7=sQuery(id+"F0.wireOp",EDGE,"E1.right");var subQ8=sQuery(id+"F0.wireOp",EDGE,"E1.top");var subQ9=sQuery(id+"F0.wireOp",EDGE,"E1.left");var subQ10=sQuery(id+"F0.wireOp",EDGE,"E23.filletArc");var subQ11=sQuery(id+"F0.wireOp",EDGE,"E24.filletArc");Q0=makeQuery(id+"F2.boolean.opBoolean","SPLIT",FACE,{"disambiguationData":[TD([makeQuery(id+"F1.opExtrude","SWEPT_FACE",FACE,{"disambiguationData":[OSD([subQ6])]})])],"derivedFrom":makeQuery(id+"F1.opExtrude","CAP_FACE",FACE,{"disambiguationData":[OSD([subQ6,subQ8,subQ9,subQ7,subQ4,subQ3,subQ2,subQ1,subQ0,subQ5,subQ10,subQ11])],"isStart":true})});}
            var sketch = newSketch(context, id + "F16", { "sketchPlane" : qUnion([Q0])});
            skSolve(sketch);
        }
        {
            var Q0;
            Q0=makeQuery(id+"F16.imprint","IMPRINT",FACE,{"disambiguationData":[TD([[makeQuery(id+"F16.imprint","IMPRINT",EDGE,{"derivedFrom":makeQuery(id+"F1.opExtrude","CAP_EDGE",EDGE,{"disambiguationData":[OSD([sQuery(id+"F0.wireOp",EDGE,"E1.bottom")])],"isStart":true})}),1.0]])]});
            var sketch = newSketch(context, id + "F17", { "sketchPlane" : qUnion([Q0])});
            skLineSegment(sketch, "E79.0", {"start": v(-70, 90) * mm, "end": v(70, 90) * mm});
            skArc(sketch, "E79.1", {"start": v(-70, 90) * mm, "mid": v(-77.07, 87.07) * mm, "end": v(-80, 80) * mm});
            skLineSegment(sketch, "E79.2", {"start": v(-80, -80) * mm, "end": v(-80, 80) * mm});
            skArc(sketch, "E79.3", {"start": v(-80, -80) * mm, "mid": v(-77.07, -87.07) * mm, "end": v(-70, -90) * mm});
            skLineSegment(sketch, "E79.4", {"start": v(-70, -90) * mm, "end": v(70, -90) * mm});
            skArc(sketch, "E79.5", {"start": v(70, -90) * mm, "mid": v(77.07, -87.07) * mm, "end": v(80, -80) * mm});
            skLineSegment(sketch, "E79.6", {"start": v(80, -80) * mm, "end": v(80, 80) * mm});
            skArc(sketch, "E79.7", {"start": v(80, 80) * mm, "mid": v(77.07, 87.07) * mm, "end": v(70, 90) * mm});
            skCircle(sketch, "E79.8", {"center": v(60, 67.5) * mm, "radius": 4 * mm});
            skCircle(sketch, "E79.9", {"center": v(60, -67.5) * mm, "radius": 4 * mm});
            skCircle(sketch, "E79.10", {"center": v(-60, -67.5) * mm, "radius": 4 * mm});
            skCircle(sketch, "E79.11", {"center": v(-60, 67.5) * mm, "radius": 4 * mm});
            skLineSegment(sketch, "E79.12", {"start": v(-60, 40.3) * mm, "end": v(-60, -40.3) * mm});
            skArc(sketch, "E79.13", {"start": v(-56.15, 48.18) * mm, "mid": v(-58.99, 44.68) * mm, "end": v(-60, 40.3) * mm});
            skArc(sketch, "E79.14", {"start": v(56.15, 48.18) * mm, "mid": v(0, 67.5) * mm, "end": v(-56.15, 48.18) * mm});
            skArc(sketch, "E79.15", {"start": v(60, 40.3) * mm, "mid": v(58.99, 44.68) * mm, "end": v(56.15, 48.18) * mm});
            skLineSegment(sketch, "E79.16", {"start": v(60, 40.3) * mm, "end": v(60, -40.3) * mm});
            skArc(sketch, "E79.17", {"start": v(56.15, -48.18) * mm, "mid": v(58.99, -44.68) * mm, "end": v(60, -40.3) * mm});
            skArc(sketch, "E79.18", {"start": v(-56.15, -48.18) * mm, "mid": v(0, -67.5) * mm, "end": v(56.15, -48.18) * mm});
            skArc(sketch, "E79.19", {"start": v(-60, -40.3) * mm, "mid": v(-58.99, -44.68) * mm, "end": v(-56.15, -48.18) * mm});
            skLineSegment(sketch, "E80", {"start": v(0, 90) * mm, "end": v(0, 120) * mm, "construction": true});
            skLineSegment(sketch, "E81", {"start": v(-33, 90) * mm, "end": v(-15, 108) * mm});
            skLineSegment(sketch, "E82", {"start": v(-15, 108) * mm, "end": v(-15, 120) * mm});
            skLineSegment(sketch, "E83.MirrorCS", {"start": v(15, 108) * mm, "end": v(15, 120) * mm});
            skLineSegment(sketch, "E84.MirrorCS", {"start": v(33, 90) * mm, "end": v(15, 108) * mm});
            skArc(sketch, "E85", {"start": v(15, 120) * mm, "mid": v(0, 135) * mm, "end": v(-15, 120) * mm});
            skCircle(sketch, "E86", {"center": v(0, 120) * mm, "radius": 6 * mm});
            skLineSegment(sketch, "E87", {"start": v(-80, 0) * mm, "end": v(80, 0) * mm, "construction": true});
            skLineSegment(sketch, "E88.MirrorCS", {"start": v(-33, -90) * mm, "end": v(-15, -108) * mm});
            skLineSegment(sketch, "E89.MirrorCS", {"start": v(-15, -108) * mm, "end": v(-15, -120) * mm});
            skArc(sketch, "E90.MirrorCS", {"start": v(15, -120) * mm, "mid": v(0, -135) * mm, "end": v(-15, -120) * mm});
            skLineSegment(sketch, "E91.MirrorCS", {"start": v(15, -108) * mm, "end": v(15, -120) * mm});
            skLineSegment(sketch, "E92.MirrorCS", {"start": v(33, -90) * mm, "end": v(15, -108) * mm});
            skCircle(sketch, "E93.MirrorC", {"center": v(0, -120) * mm, "radius": 6 * mm});
            skLineSegment(sketch, "E94.MirrorCS", {"start": v(0, -90) * mm, "end": v(0, -120) * mm, "construction": true});
            skSolve(sketch);
        }
        {
            var Q0;
            Q0 = qSketchRegion(id + "F17", true);
            var Q1;
            Q1=makeQuery(id+"F2.opExtrude","CAP_FACE",FACE,{"disambiguationData":[OSD([sQuery(id+"F0.wireOp",EDGE,"E12"),sQuery(id+"F0.wireOp",EDGE,"E13"),sQuery(id+"F0.wireOp",EDGE,"E14"),sQuery(id+"F0.wireOp",EDGE,"E15"),sQuery(id+"F0.wireOp",EDGE,"E17.filletArc"),sQuery(id+"F0.wireOp",EDGE,"E18.filletArc"),sQuery(id+"F0.wireOp",EDGE,"E19.filletArc"),sQuery(id+"F0.wireOp",EDGE,"E20.filletArc"),sQuery(id+"F0.wireOp",EDGE,"E25.0"),sQuery(id+"F0.wireOp",EDGE,"E25.1"),sQuery(id+"F0.wireOp",EDGE,"E25.2"),sQuery(id+"F0.wireOp",EDGE,"E25.3"),sQuery(id+"F0.wireOp",EDGE,"E25.4"),sQuery(id+"F0.wireOp",EDGE,"E25.5"),sQuery(id+"F0.wireOp",EDGE,"E25.6"),sQuery(id+"F0.wireOp",EDGE,"E25.7")])],"isStart":false});
            extrude(context, id + "F18", {"entities" : qUnion([Q0]), "endBound" : BoundingType.UP_TO_SURFACE, "endBoundEntityFace" : qUnion([Q1]), "depth" : 25 * mm});
        }
    });
